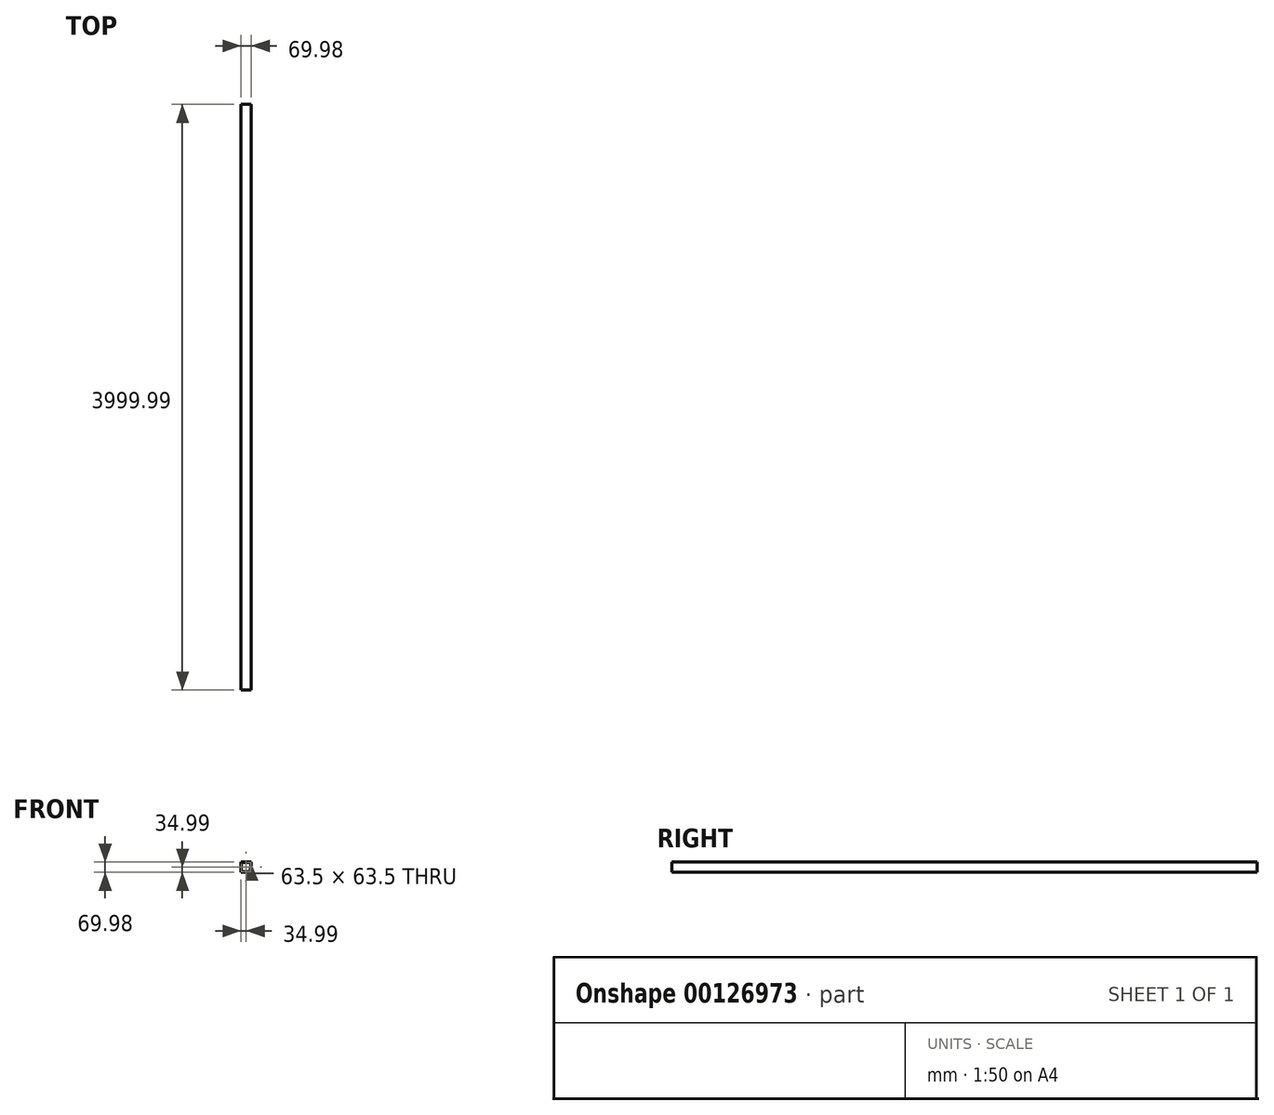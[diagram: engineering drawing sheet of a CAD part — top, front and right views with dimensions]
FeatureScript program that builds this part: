
annotation { "Feature Type Name" : "Feature", "Feature Type Description" : "" }
export const myFeature = defineFeature(function(context is Context, id is Id, definition is map)
    precondition{}
    {
        {
            var Q0;
            Q0=qCreatedBy(makeId("Front.planeOp"),FACE);
            var sketch = newSketch(context, id + "F0", { "sketchPlane" : qUnion([Q0])});
            skLineSegment(sketch, "E0.bottom", {"start": v(34.99, 34.99) * mm, "end": v(-34.99, 34.99) * mm});
            skLineSegment(sketch, "E0.top", {"start": v(34.99, -34.99) * mm, "end": v(-34.99, -34.99) * mm});
            skLineSegment(sketch, "E0.left", {"start": v(34.99, 34.99) * mm, "end": v(34.99, -34.99) * mm});
            skLineSegment(sketch, "E0.right", {"start": v(-34.99, 34.99) * mm, "end": v(-34.99, -34.99) * mm});
            skPoint(sketch, "E0.middle", {"position": v(0, 0) * mm});
            skLineSegment(sketch, "E1.bottom", {"start": v(31.75, 31.75) * mm, "end": v(-31.75, 31.75) * mm});
            skLineSegment(sketch, "E1.top", {"start": v(31.75, -31.75) * mm, "end": v(-31.75, -31.75) * mm});
            skLineSegment(sketch, "E1.left", {"start": v(31.75, 31.75) * mm, "end": v(31.75, -31.75) * mm});
            skLineSegment(sketch, "E1.right", {"start": v(-31.75, 31.75) * mm, "end": v(-31.75, -31.75) * mm});
            skSolve(sketch);
        }
        {
            var Q0;
            Q0=makeQuery(id+"F0.imprint","IMPRINT",FACE,{"disambiguationData":[TD([[makeQuery(id+"F0.imprint","IMPRINT",EDGE,{"derivedFrom":sQuery(id+"F0.wireOp",EDGE,"E0.bottom")}),1.0]])]});
            extrude(context, id + "F1", {"entities" : qUnion([Q0]), "depth" : 4000 * mm});
        }
    });
